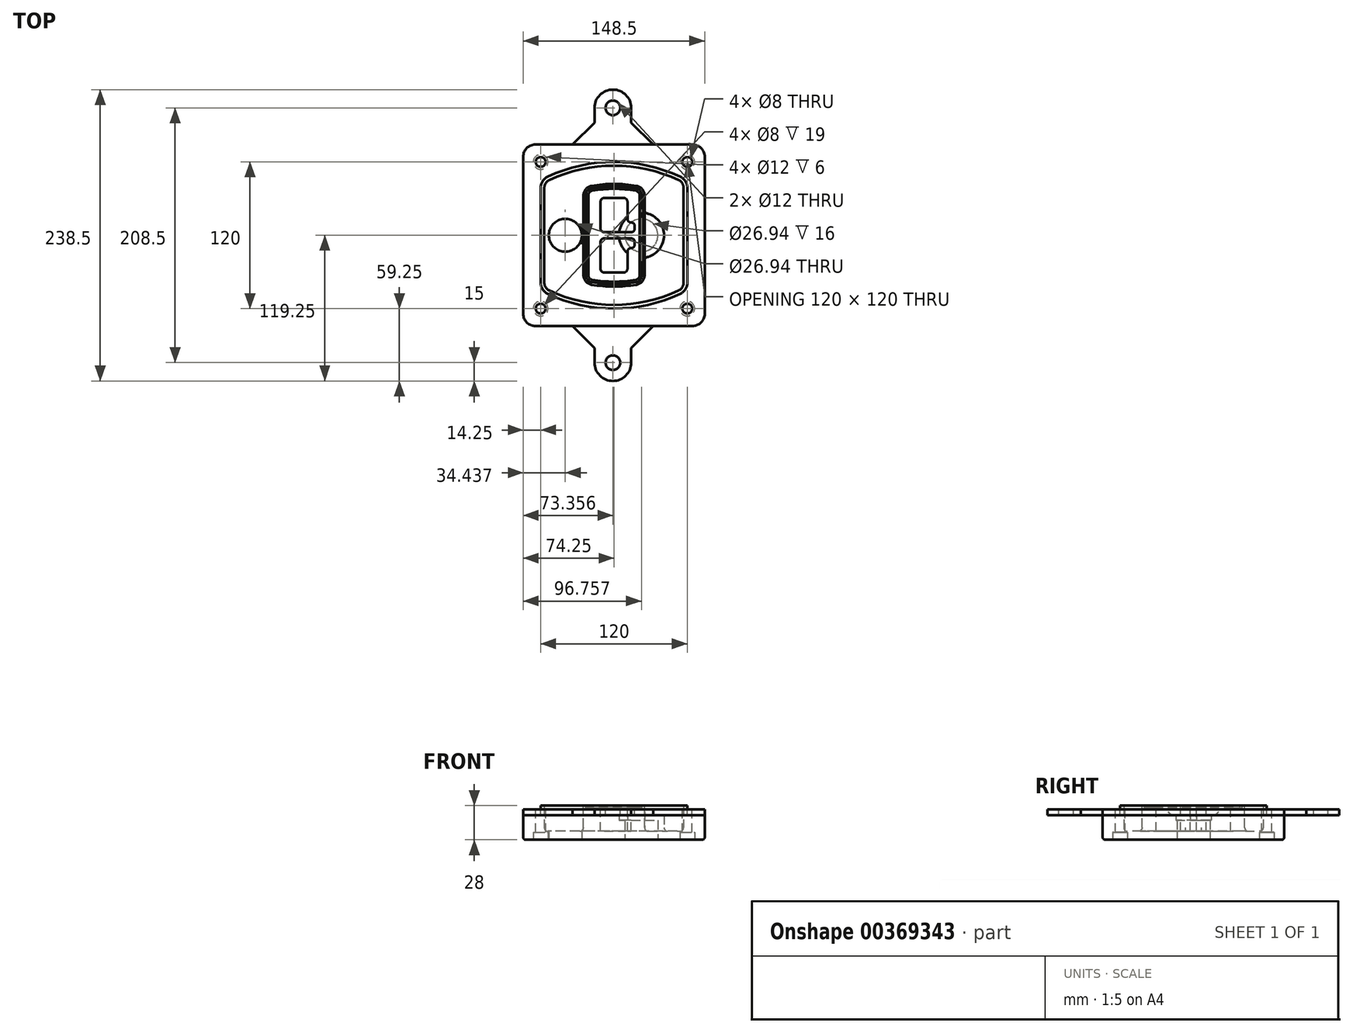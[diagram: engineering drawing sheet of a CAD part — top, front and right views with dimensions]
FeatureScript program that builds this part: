
annotation { "Feature Type Name" : "Feature", "Feature Type Description" : "" }
export const myFeature = defineFeature(function(context is Context, id is Id, definition is map)
    precondition{}
    {
        {
            var Q0;
            Q0=qCreatedBy(makeId("Top.planeOp"),FACE);
            var sketch = newSketch(context, id + "F0", { "sketchPlane" : qUnion([Q0])});
            skPoint(sketch, "E0.rect.middle", {"position": v(0, 0) * mm});
            skLineSegment(sketch, "E1.bottom", {"start": v(-64.25, -74.25) * mm, "end": v(64.25, -74.25) * mm});
            skLineSegment(sketch, "E1.top", {"start": v(-64.25, 74.25) * mm, "end": v(64.25, 74.25) * mm});
            skLineSegment(sketch, "E1.left", {"start": v(-74.25, -64.25) * mm, "end": v(-74.25, 64.25) * mm});
            skLineSegment(sketch, "E1.right", {"start": v(74.25, -64.25) * mm, "end": v(74.25, 64.25) * mm});
            skLineSegment(sketch, "E2", {"start": v(-74.25, 74.25) * mm, "end": v(74.25, -74.25) * mm, "construction": true});
            skLineSegment(sketch, "E3", {"start": v(74.25, 74.25) * mm, "end": v(-74.25, -74.25) * mm, "construction": true});
            skCircle(sketch, "E4", {"center": v(-60, 60) * mm, "radius": 4 * mm});
            skCircle(sketch, "E5", {"center": v(60, 60) * mm, "radius": 4 * mm});
            skCircle(sketch, "E6", {"center": v(60, -60) * mm, "radius": 4 * mm});
            skCircle(sketch, "E7", {"center": v(-60, -60) * mm, "radius": 4 * mm});
            skLineSegment(sketch, "E8", {"start": v(-60, 60) * mm, "end": v(60, 60) * mm, "construction": true});
            skLineSegment(sketch, "E9", {"start": v(60, 60) * mm, "end": v(60, -60) * mm, "construction": true});
            skLineSegment(sketch, "E10", {"start": v(60, -60) * mm, "end": v(-60, -60) * mm, "construction": true});
            skLineSegment(sketch, "E11", {"start": v(-60, -60) * mm, "end": v(-60, 60) * mm, "construction": true});
            skLineSegment(sketch, "E12", {"start": v(-60, 38.83) * mm, "end": v(-60, -38.83) * mm});
            skLineSegment(sketch, "E13", {"start": v(60, 38.83) * mm, "end": v(60, -38.83) * mm});
            skArc(sketch, "E14", {"start": v(54.26, 47.88) * mm, "mid": v(0, 60) * mm, "end": v(-54.26, 47.88) * mm});
            skArc(sketch, "E15", {"start": v(-54.26, -47.88) * mm, "mid": v(0, -60) * mm, "end": v(54.26, -47.88) * mm});
            skLineSegment(sketch, "E16", {"start": v(-60, 0) * mm, "end": v(60, 0) * mm, "construction": true});
            skPoint(sketch, "E17.visualSharp", {"position": v(-60, -45) * mm});
            skArc(sketch, "E17.filletArc", {"start": v(-60, -38.83) * mm, "mid": v(-58.44, -44.2) * mm, "end": v(-54.26, -47.88) * mm});
            skPoint(sketch, "E18.visualSharp", {"position": v(-60, 45) * mm});
            skArc(sketch, "E18.filletArc", {"start": v(-54.26, 47.88) * mm, "mid": v(-58.44, 44.2) * mm, "end": v(-60, 38.83) * mm});
            skPoint(sketch, "E19.visualSharp", {"position": v(60, 45) * mm});
            skArc(sketch, "E19.filletArc", {"start": v(60, 38.83) * mm, "mid": v(58.44, 44.2) * mm, "end": v(54.26, 47.88) * mm});
            skPoint(sketch, "E20.visualSharp", {"position": v(60, -45) * mm});
            skArc(sketch, "E20.filletArc", {"start": v(54.26, -47.88) * mm, "mid": v(58.44, -44.2) * mm, "end": v(60, -38.83) * mm});
            skPoint(sketch, "E21.visualSharp", {"position": v(-74.25, 74.25) * mm});
            skArc(sketch, "E21.filletArc", {"start": v(-64.25, 74.25) * mm, "mid": v(-71.32, 71.32) * mm, "end": v(-74.25, 64.25) * mm});
            skPoint(sketch, "E22.visualSharp", {"position": v(74.25, 74.25) * mm});
            skArc(sketch, "E22.filletArc", {"start": v(74.25, 64.25) * mm, "mid": v(71.32, 71.32) * mm, "end": v(64.25, 74.25) * mm});
            skPoint(sketch, "E23.visualSharp", {"position": v(74.25, -74.25) * mm});
            skArc(sketch, "E23.filletArc", {"start": v(64.25, -74.25) * mm, "mid": v(71.32, -71.32) * mm, "end": v(74.25, -64.25) * mm});
            skPoint(sketch, "E24.visualSharp", {"position": v(-74.25, -74.25) * mm});
            skArc(sketch, "E24.filletArc", {"start": v(-74.25, -64.25) * mm, "mid": v(-71.32, -71.32) * mm, "end": v(-64.25, -74.25) * mm});
            skArc(sketch, "E25.0", {"start": v(57, 38.83) * mm, "mid": v(55.9, 42.58) * mm, "end": v(52.98, 45.17) * mm});
            skLineSegment(sketch, "E25.1", {"start": v(57, 38.83) * mm, "end": v(57, -38.83) * mm});
            skArc(sketch, "E25.2", {"start": v(52.98, -45.17) * mm, "mid": v(55.9, -42.58) * mm, "end": v(57, -38.83) * mm});
            skArc(sketch, "E25.3", {"start": v(-52.98, -45.17) * mm, "mid": v(0, -57) * mm, "end": v(52.98, -45.17) * mm});
            skArc(sketch, "E25.4", {"start": v(-57, -38.83) * mm, "mid": v(-55.9, -42.58) * mm, "end": v(-52.98, -45.17) * mm});
            skArc(sketch, "E25.5", {"start": v(52.98, 45.17) * mm, "mid": v(0, 57) * mm, "end": v(-52.98, 45.17) * mm});
            skLineSegment(sketch, "E25.6", {"start": v(-57, 38.83) * mm, "end": v(-57, -38.83) * mm});
            skArc(sketch, "E25.7", {"start": v(-52.98, 45.17) * mm, "mid": v(-55.9, 42.58) * mm, "end": v(-57, 38.83) * mm});
            skArc(sketch, "E26.0", {"start": v(-55.96, 51.5) * mm, "mid": v(-61.82, 46.33) * mm, "end": v(-64, 38.83) * mm});
            skArc(sketch, "E26.1", {"start": v(55.96, 51.5) * mm, "mid": v(0, 64) * mm, "end": v(-55.96, 51.5) * mm});
            skArc(sketch, "E26.2", {"start": v(64, 38.83) * mm, "mid": v(61.82, 46.33) * mm, "end": v(55.96, 51.5) * mm});
            skLineSegment(sketch, "E26.3", {"start": v(64, 38.83) * mm, "end": v(64, -38.83) * mm});
            skArc(sketch, "E26.4", {"start": v(55.96, -51.5) * mm, "mid": v(61.82, -46.33) * mm, "end": v(64, -38.83) * mm});
            skLineSegment(sketch, "E26.5", {"start": v(-64, 38.83) * mm, "end": v(-64, -38.83) * mm});
            skArc(sketch, "E26.6", {"start": v(-55.96, -51.5) * mm, "mid": v(0, -64) * mm, "end": v(55.96, -51.5) * mm});
            skArc(sketch, "E26.7", {"start": v(-64, -38.83) * mm, "mid": v(-61.82, -46.33) * mm, "end": v(-55.96, -51.5) * mm});
            skSolve(sketch);
        }
        {
            var Q0;
            Q0=makeQuery(id+"F0.imprint","IMPRINT",FACE,{"disambiguationData":[TD([[makeQuery(id+"F0.imprint","IMPRINT",EDGE,{"derivedFrom":sQuery(id+"F0.wireOp",EDGE,"E1.bottom")}),1.0]])]});
            var Q1;
            Q1=makeQuery(id+"F0.imprint","IMPRINT",FACE,{"disambiguationData":[TD([[makeQuery(id+"F0.imprint","IMPRINT",EDGE,{"derivedFrom":sQuery(id+"F0.wireOp",EDGE,"E12")}),1.0]])]});
            var Q2;
            Q2=makeQuery(id+"F0.imprint","IMPRINT",FACE,{"disambiguationData":[TD([[makeQuery(id+"F0.imprint","IMPRINT",EDGE,{"derivedFrom":sQuery(id+"F0.wireOp",EDGE,"E25.0")}),1.0]])]});
            var Q3;
            Q3=makeQuery(id+"F0.imprint","IMPRINT",FACE,{"disambiguationData":[TD([[makeQuery(id+"F0.imprint","IMPRINT",EDGE,{"derivedFrom":sQuery(id+"F0.wireOp",EDGE,"E12")}),-1.0]])]});
            extrude(context, id + "F1", {"entities" : qUnion([Q0, Q1, Q2, Q3]), "oppositeDirection" : true, "depth" : 25 * mm});
        }
        {
            var Q0;
            Q0=makeQuery(id+"F0.imprint","IMPRINT",FACE,{"disambiguationData":[TD([[makeQuery(id+"F0.imprint","IMPRINT",EDGE,{"derivedFrom":sQuery(id+"F0.wireOp",EDGE,"E12")}),1.0]])]});
            extrude(context, id + "F2", {"entities" : qUnion([Q0]), "operationType" : NewBodyOperationType.ADD, "depth" : 3 * mm});
        }
        {
            var Q0;
            Q0=makeQuery(id+"F0.imprint","IMPRINT",FACE,{"disambiguationData":[TD([[makeQuery(id+"F0.imprint","IMPRINT",EDGE,{"derivedFrom":sQuery(id+"F0.wireOp",EDGE,"E25.0")}),1.0]])]});
            extrude(context, id + "F3", {"entities" : qUnion([Q0]), "operationType" : NewBodyOperationType.REMOVE, "oppositeDirection" : true, "depth" : 18 * mm});
        }
        {
            var Q0;
            Q0=makeQuery(id+"F2.opExtrude","CAP_FACE",FACE,{"disambiguationData":[OSD([sQuery(id+"F0.wireOp",EDGE,"E12"),sQuery(id+"F0.wireOp",EDGE,"E13"),sQuery(id+"F0.wireOp",EDGE,"E14"),sQuery(id+"F0.wireOp",EDGE,"E15"),sQuery(id+"F0.wireOp",EDGE,"E17.filletArc"),sQuery(id+"F0.wireOp",EDGE,"E18.filletArc"),sQuery(id+"F0.wireOp",EDGE,"E19.filletArc"),sQuery(id+"F0.wireOp",EDGE,"E20.filletArc"),sQuery(id+"F0.wireOp",EDGE,"E25.0"),sQuery(id+"F0.wireOp",EDGE,"E25.1"),sQuery(id+"F0.wireOp",EDGE,"E25.2"),sQuery(id+"F0.wireOp",EDGE,"E25.3"),sQuery(id+"F0.wireOp",EDGE,"E25.4"),sQuery(id+"F0.wireOp",EDGE,"E25.5"),sQuery(id+"F0.wireOp",EDGE,"E25.6"),sQuery(id+"F0.wireOp",EDGE,"E25.7")])],"isStart":false});
            var sketch = newSketch(context, id + "F4", { "sketchPlane" : qUnion([Q0])});
            skArc(sketch, "E27.0", {"start": v(-18.34, -40.45) * mm, "mid": v(0, -42) * mm, "end": v(18.34, -40.45) * mm});
            skArc(sketch, "E28.0", {"start": v(18.34, 40.45) * mm, "mid": v(0, 42) * mm, "end": v(-18.34, 40.45) * mm});
            skLineSegment(sketch, "E29", {"start": v(-25, 32.57) * mm, "end": v(-25, -32.57) * mm});
            skLineSegment(sketch, "E30", {"start": v(25, 32.57) * mm, "end": v(25, -32.57) * mm});
            skLineSegment(sketch, "E31", {"start": v(-25, 39.1) * mm, "end": v(25, 39.1) * mm, "construction": true});
            skLineSegment(sketch, "E32", {"start": v(-25, -39.1) * mm, "end": v(25, -39.1) * mm, "construction": true});
            skPoint(sketch, "E33.visualSharp", {"position": v(-25, 39.1) * mm});
            skArc(sketch, "E33.filletArc", {"start": v(-18.34, 40.45) * mm, "mid": v(-23.11, 37.73) * mm, "end": v(-25, 32.57) * mm});
            skPoint(sketch, "E34.visualSharp", {"position": v(25, 39.1) * mm});
            skArc(sketch, "E34.filletArc", {"start": v(25, 32.57) * mm, "mid": v(23.11, 37.73) * mm, "end": v(18.34, 40.45) * mm});
            skPoint(sketch, "E35.visualSharp", {"position": v(25, -39.1) * mm});
            skArc(sketch, "E35.filletArc", {"start": v(18.34, -40.45) * mm, "mid": v(23.11, -37.73) * mm, "end": v(25, -32.57) * mm});
            skPoint(sketch, "E36.visualSharp", {"position": v(-25, -39.1) * mm});
            skArc(sketch, "E36.filletArc", {"start": v(-25, -32.57) * mm, "mid": v(-23.11, -37.73) * mm, "end": v(-18.34, -40.45) * mm});
            skArc(sketch, "E37.0", {"start": v(52.98, 45.17) * mm, "mid": v(0, 57) * mm, "end": v(-52.98, 45.17) * mm});
            skArc(sketch, "E37.1", {"start": v(-52.98, 45.17) * mm, "mid": v(-55.9, 42.58) * mm, "end": v(-57, 38.83) * mm});
            skLineSegment(sketch, "E37.2", {"start": v(-57, 38.83) * mm, "end": v(-57, -38.83) * mm});
            skArc(sketch, "E37.3", {"start": v(-57, -38.83) * mm, "mid": v(-55.9, -42.58) * mm, "end": v(-52.98, -45.17) * mm});
            skArc(sketch, "E37.4", {"start": v(-52.98, -45.17) * mm, "mid": v(0, -57) * mm, "end": v(52.98, -45.17) * mm});
            skArc(sketch, "E37.5", {"start": v(52.98, -45.17) * mm, "mid": v(55.9, -42.58) * mm, "end": v(57, -38.83) * mm});
            skLineSegment(sketch, "E37.6", {"start": v(57, 38.83) * mm, "end": v(57, -38.83) * mm});
            skArc(sketch, "E37.7", {"start": v(57, 38.83) * mm, "mid": v(55.9, 42.58) * mm, "end": v(52.98, 45.17) * mm});
            skLineSegment(sketch, "E38.0", {"start": v(23, 32.57) * mm, "end": v(23, -32.57) * mm});
            skArc(sketch, "E38.1", {"start": v(18, -38.48) * mm, "mid": v(21.58, -36.44) * mm, "end": v(23, -32.57) * mm});
            skArc(sketch, "E38.2", {"start": v(-18, -38.48) * mm, "mid": v(0, -40) * mm, "end": v(18, -38.48) * mm});
            skArc(sketch, "E38.3", {"start": v(-23, -32.57) * mm, "mid": v(-21.58, -36.44) * mm, "end": v(-18, -38.48) * mm});
            skLineSegment(sketch, "E38.4", {"start": v(-23, 32.57) * mm, "end": v(-23, -32.57) * mm});
            skArc(sketch, "E38.5", {"start": v(23, 32.57) * mm, "mid": v(21.58, 36.44) * mm, "end": v(18, 38.48) * mm});
            skArc(sketch, "E38.6", {"start": v(-18, 38.48) * mm, "mid": v(-21.58, 36.44) * mm, "end": v(-23, 32.57) * mm});
            skArc(sketch, "E38.7", {"start": v(18, 38.48) * mm, "mid": v(0, 40) * mm, "end": v(-18, 38.48) * mm});
            skArc(sketch, "E39.0", {"start": v(21, 32.57) * mm, "mid": v(20.06, 35.15) * mm, "end": v(17.67, 36.5) * mm});
            skLineSegment(sketch, "E39.1", {"start": v(21, 32.57) * mm, "end": v(21, -32.57) * mm});
            skArc(sketch, "E39.2", {"start": v(17.67, -36.5) * mm, "mid": v(20.06, -35.15) * mm, "end": v(21, -32.57) * mm});
            skArc(sketch, "E39.3", {"start": v(-17.67, -36.5) * mm, "mid": v(0, -38) * mm, "end": v(17.67, -36.5) * mm});
            skArc(sketch, "E39.4", {"start": v(-21, -32.57) * mm, "mid": v(-20.06, -35.15) * mm, "end": v(-17.67, -36.5) * mm});
            skArc(sketch, "E39.5", {"start": v(17.67, 36.5) * mm, "mid": v(0, 38) * mm, "end": v(-17.67, 36.5) * mm});
            skLineSegment(sketch, "E39.6", {"start": v(-21, 32.57) * mm, "end": v(-21, -32.57) * mm});
            skArc(sketch, "E39.7", {"start": v(-17.67, 36.5) * mm, "mid": v(-20.06, 35.15) * mm, "end": v(-21, 32.57) * mm});
            skLineSegment(sketch, "E40", {"start": v(-25, 0) * mm, "end": v(25, 0) * mm, "construction": true});
            skLineSegment(sketch, "E41", {"start": v(-11, 5.5) * mm, "end": v(-11, 27.5) * mm});
            skLineSegment(sketch, "E42", {"start": v(-8, 30.5) * mm, "end": v(8, 30.5) * mm});
            skLineSegment(sketch, "E43", {"start": v(11, 27.5) * mm, "end": v(11, 13.5) * mm});
            skLineSegment(sketch, "E44", {"start": v(14, 10.5) * mm, "end": v(14, 10.5) * mm});
            skLineSegment(sketch, "E45", {"start": v(17, 7.5) * mm, "end": v(17, 5.5) * mm});
            skLineSegment(sketch, "E46", {"start": v(14, 2.5) * mm, "end": v(-8, 2.5) * mm});
            skPoint(sketch, "E47.visualSharp", {"position": v(-11, 30.5) * mm});
            skArc(sketch, "E47.filletArc", {"start": v(-8, 30.5) * mm, "mid": v(-10.12, 29.62) * mm, "end": v(-11, 27.5) * mm});
            skPoint(sketch, "E48.visualSharp", {"position": v(11, 30.5) * mm});
            skArc(sketch, "E48.filletArc", {"start": v(11, 27.5) * mm, "mid": v(10.12, 29.62) * mm, "end": v(8, 30.5) * mm});
            skPoint(sketch, "E49.visualSharp", {"position": v(11, 10.5) * mm});
            skArc(sketch, "E49.filletArc", {"start": v(11, 13.5) * mm, "mid": v(11.88, 11.38) * mm, "end": v(14, 10.5) * mm});
            skPoint(sketch, "E50.visualSharp", {"position": v(17, 10.5) * mm});
            skArc(sketch, "E50.filletArc", {"start": v(17, 7.5) * mm, "mid": v(16.12, 9.62) * mm, "end": v(14, 10.5) * mm});
            skPoint(sketch, "E51.visualSharp", {"position": v(17, 2.5) * mm});
            skArc(sketch, "E51.filletArc", {"start": v(14, 2.5) * mm, "mid": v(16.12, 3.38) * mm, "end": v(17, 5.5) * mm});
            skPoint(sketch, "E52.visualSharp", {"position": v(-11, 2.5) * mm});
            skArc(sketch, "E52.filletArc", {"start": v(-11, 5.5) * mm, "mid": v(-10.12, 3.38) * mm, "end": v(-8, 2.5) * mm});
            skLineSegment(sketch, "E53.0.MirrorCS", {"start": v(14, -2.5) * mm, "end": v(-8, -2.5) * mm});
            skArc(sketch, "E54.0.MirrorCS", {"start": v(-11, -5.5) * mm, "mid": v(-10.12, -3.38) * mm, "end": v(-8, -2.5) * mm});
            skLineSegment(sketch, "E55.0.MirrorCS", {"start": v(-11, -5.5) * mm, "end": v(-11, -27.5) * mm});
            skArc(sketch, "E56.0.MirrorCS", {"start": v(-8, -30.5) * mm, "mid": v(-10.12, -29.62) * mm, "end": v(-11, -27.5) * mm});
            skLineSegment(sketch, "E57.0.MirrorCS", {"start": v(-8, -30.5) * mm, "end": v(8, -30.5) * mm});
            skArc(sketch, "E58.0.MirrorCS", {"start": v(11, -27.5) * mm, "mid": v(10.12, -29.62) * mm, "end": v(8, -30.5) * mm});
            skLineSegment(sketch, "E59.0.MirrorCS", {"start": v(11, -27.5) * mm, "end": v(11, -13.5) * mm});
            skArc(sketch, "E60.0.MirrorCS", {"start": v(11, -13.5) * mm, "mid": v(11.88, -11.38) * mm, "end": v(14, -10.5) * mm});
            skArc(sketch, "E61.0.MirrorCS", {"start": v(17, -7.5) * mm, "mid": v(16.12, -9.62) * mm, "end": v(14, -10.5) * mm});
            skLineSegment(sketch, "E62.0.MirrorCS", {"start": v(17, -7.5) * mm, "end": v(17, -5.5) * mm});
            skArc(sketch, "E63.0.MirrorCS", {"start": v(14, -2.5) * mm, "mid": v(16.12, -3.38) * mm, "end": v(17, -5.5) * mm});
            skSolve(sketch);
        }
        {
            var Q0;
            Q0=makeQuery(id+"F4.imprint","IMPRINT",FACE,{"disambiguationData":[TD([[makeQuery(id+"F4.imprint","IMPRINT",EDGE,{"derivedFrom":sQuery(id+"F4.wireOp",EDGE,"E27.0")}),1.0]])]});
            var Q1;
            Q1=makeQuery(id+"F4.imprint","IMPRINT",FACE,{"disambiguationData":[TD([[makeQuery(id+"F4.imprint","IMPRINT",EDGE,{"derivedFrom":sQuery(id+"F4.wireOp",EDGE,"E38.0")}),-1.0]])]});
            var Q2;
            Q2=makeQuery(id+"F4.imprint","IMPRINT",FACE,{"disambiguationData":[TD([[makeQuery(id+"F4.imprint","IMPRINT",EDGE,{"derivedFrom":sQuery(id+"F4.wireOp",EDGE,"E39.0")}),1.0]])]});
            extrude(context, id + "F5", {"entities" : qUnion([Q0, Q1, Q2]), "operationType" : NewBodyOperationType.ADD, "endBound" : BoundingType.UP_TO_NEXT, "oppositeDirection" : true, "depth" : 25 * mm});
        }
        {
            var Q0;
            Q0=makeQuery(id+"F4.imprint","IMPRINT",FACE,{"disambiguationData":[TD([[makeQuery(id+"F4.imprint","IMPRINT",EDGE,{"derivedFrom":sQuery(id+"F4.wireOp",EDGE,"E38.0")}),-1.0]])]});
            extrude(context, id + "F6", {"entities" : qUnion([Q0]), "operationType" : NewBodyOperationType.REMOVE, "oppositeDirection" : true, "depth" : 2 * mm});
        }
        {
            var Q0;
            Q0=makeQuery(id+"F1.opExtrude","CAP_FACE",FACE,{"disambiguationData":[OSD([sQuery(id+"F0.wireOp",EDGE,"E1.bottom"),sQuery(id+"F0.wireOp",EDGE,"E1.top"),sQuery(id+"F0.wireOp",EDGE,"E1.left"),sQuery(id+"F0.wireOp",EDGE,"E1.right"),sQuery(id+"F0.wireOp",EDGE,"E4"),sQuery(id+"F0.wireOp",EDGE,"E5"),sQuery(id+"F0.wireOp",EDGE,"E6"),sQuery(id+"F0.wireOp",EDGE,"E7"),sQuery(id+"F0.wireOp",EDGE,"E21.filletArc"),sQuery(id+"F0.wireOp",EDGE,"E22.filletArc"),sQuery(id+"F0.wireOp",EDGE,"E23.filletArc"),sQuery(id+"F0.wireOp",EDGE,"E24.filletArc")])],"isStart":false});
            var sketch = newSketch(context, id + "F7", { "sketchPlane" : qUnion([Q0])});
            skCircle(sketch, "E64", {"center": v(22.5, 0) * mm, "radius": 13.47 * mm});
            skCircle(sketch, "E65", {"center": v(-39.81, 0) * mm, "radius": 13.47 * mm});
            skLineSegment(sketch, "E66", {"start": v(74.25, 0) * mm, "end": v(-74.25, 0) * mm});
            skCircle(sketch, "E67", {"center": v(22.5, 0) * mm, "radius": 18.47 * mm});
            skCircle(sketch, "E68", {"center": v(60, -60) * mm, "radius": 6 * mm});
            skCircle(sketch, "E69", {"center": v(-60, -60) * mm, "radius": 6 * mm});
            skCircle(sketch, "E70", {"center": v(-60, 60) * mm, "radius": 6 * mm});
            skCircle(sketch, "E71", {"center": v(60, 60) * mm, "radius": 6 * mm});
            skSolve(sketch);
        }
        {
            var Q0;
            {var subQ1=sQuery(id+"F7.wireOp",EDGE,"E66");var subQ4=sQuery(id+"F7.wireOp",EDGE,"E64");var subQ6=makeQuery(id+"F7.imprint","INTERSECT",VERTEX,{"disambiguationData":[OD(0.0)],"derivedFrom":[subQ4,subQ1]});Q0=makeQuery(id+"F7.imprint","IMPRINT",FACE,{"disambiguationData":[TD([[makeQuery(id+"F7.imprint","IMPRINT",EDGE,{"disambiguationData":[TD([[subQ6,-1.0]])],"derivedFrom":subQ4}),-1.0]])]});}
            var Q1;
            {var subQ0=sQuery(id+"F7.wireOp",EDGE,"E66");var subQ1=sQuery(id+"F7.wireOp",EDGE,"E64");var subQ3=makeQuery(id+"F7.imprint","INTERSECT",VERTEX,{"disambiguationData":[OD(0.0)],"derivedFrom":[subQ1,subQ0]});Q1=makeQuery(id+"F7.imprint","IMPRINT",FACE,{"disambiguationData":[TD([[makeQuery(id+"F7.imprint","IMPRINT",EDGE,{"disambiguationData":[TD([[subQ3,-1.0]])],"derivedFrom":subQ1}),1.0]])]});}
            var Q2;
            {var subQ0=sQuery(id+"F7.wireOp",EDGE,"E66");var subQ1=sQuery(id+"F7.wireOp",EDGE,"E64");var subQ3=makeQuery(id+"F7.imprint","INTERSECT",VERTEX,{"disambiguationData":[OD(0.0)],"derivedFrom":[subQ1,subQ0]});Q2=makeQuery(id+"F7.imprint","IMPRINT",FACE,{"disambiguationData":[TD([[makeQuery(id+"F7.imprint","IMPRINT",EDGE,{"disambiguationData":[TD([[subQ3,1.0]])],"derivedFrom":subQ1}),1.0]])]});}
            var Q3;
            {var subQ1=sQuery(id+"F7.wireOp",EDGE,"E66");var subQ4=sQuery(id+"F7.wireOp",EDGE,"E64");var subQ6=makeQuery(id+"F7.imprint","INTERSECT",VERTEX,{"disambiguationData":[OD(0.0)],"derivedFrom":[subQ4,subQ1]});Q3=makeQuery(id+"F7.imprint","IMPRINT",FACE,{"disambiguationData":[TD([[makeQuery(id+"F7.imprint","IMPRINT",EDGE,{"disambiguationData":[TD([[subQ6,1.0]])],"derivedFrom":subQ4}),-1.0]])]});}
            extrude(context, id + "F8", {"entities" : qUnion([Q0, Q1, Q2, Q3]), "operationType" : NewBodyOperationType.ADD, "oppositeDirection" : true, "depth" : 20 * mm});
        }
        {
            var Q0;
            {var subQ0=sQuery(id+"F7.wireOp",EDGE,"E66");var subQ1=sQuery(id+"F7.wireOp",EDGE,"E64");var subQ3=makeQuery(id+"F7.imprint","INTERSECT",VERTEX,{"disambiguationData":[OD(0.0)],"derivedFrom":[subQ1,subQ0]});Q0=makeQuery(id+"F7.imprint","IMPRINT",FACE,{"disambiguationData":[TD([[makeQuery(id+"F7.imprint","IMPRINT",EDGE,{"disambiguationData":[TD([[subQ3,-1.0]])],"derivedFrom":subQ1}),1.0]])]});}
            var Q1;
            {var subQ0=sQuery(id+"F7.wireOp",EDGE,"E66");var subQ1=sQuery(id+"F7.wireOp",EDGE,"E64");var subQ3=makeQuery(id+"F7.imprint","INTERSECT",VERTEX,{"disambiguationData":[OD(0.0)],"derivedFrom":[subQ1,subQ0]});Q1=makeQuery(id+"F7.imprint","IMPRINT",FACE,{"disambiguationData":[TD([[makeQuery(id+"F7.imprint","IMPRINT",EDGE,{"disambiguationData":[TD([[subQ3,1.0]])],"derivedFrom":subQ1}),1.0]])]});}
            extrude(context, id + "F9", {"entities" : qUnion([Q0, Q1]), "operationType" : NewBodyOperationType.REMOVE, "oppositeDirection" : true, "depth" : 16 * mm});
        }
        {
            var Q0;
            {var subQ0=sQuery(id+"F7.wireOp",EDGE,"E66");var subQ1=sQuery(id+"F7.wireOp",EDGE,"E65");var subQ3=makeQuery(id+"F7.imprint","INTERSECT",VERTEX,{"disambiguationData":[OD(0.0)],"derivedFrom":[subQ1,subQ0]});Q0=makeQuery(id+"F7.imprint","IMPRINT",FACE,{"disambiguationData":[TD([[makeQuery(id+"F7.imprint","IMPRINT",EDGE,{"disambiguationData":[TD([[subQ3,-1.0]])],"derivedFrom":subQ1}),1.0]])]});}
            var Q1;
            {var subQ0=sQuery(id+"F7.wireOp",EDGE,"E66");var subQ1=sQuery(id+"F7.wireOp",EDGE,"E65");var subQ3=makeQuery(id+"F7.imprint","INTERSECT",VERTEX,{"disambiguationData":[OD(0.0)],"derivedFrom":[subQ1,subQ0]});Q1=makeQuery(id+"F7.imprint","IMPRINT",FACE,{"disambiguationData":[TD([[makeQuery(id+"F7.imprint","IMPRINT",EDGE,{"disambiguationData":[TD([[subQ3,1.0]])],"derivedFrom":subQ1}),1.0]])]});}
            extrude(context, id + "F10", {"entities" : qUnion([Q0, Q1]), "operationType" : NewBodyOperationType.REMOVE, "oppositeDirection" : true, "depth" : 25 * mm});
        }
        {
            var Q0;
            Q0=makeQuery(id+"F7.imprint","IMPRINT",FACE,{"disambiguationData":[TD([[makeQuery(id+"F7.imprint","IMPRINT",EDGE,{"derivedFrom":sQuery(id+"F7.wireOp",EDGE,"E68")}),1.0]])]});
            var Q1;
            Q1=makeQuery(id+"F7.imprint","IMPRINT",FACE,{"disambiguationData":[TD([[makeQuery(id+"F7.imprint","IMPRINT",EDGE,{"derivedFrom":makeQuery(id+"F1.opExtrude","CAP_EDGE",EDGE,{"disambiguationData":[OSD([sQuery(id+"F0.wireOp",EDGE,"E5")])],"isStart":false})}),-1.0]])]});
            var Q2;
            Q2=makeQuery(id+"F7.imprint","IMPRINT",FACE,{"disambiguationData":[TD([[makeQuery(id+"F7.imprint","IMPRINT",EDGE,{"derivedFrom":sQuery(id+"F7.wireOp",EDGE,"E69")}),1.0]])]});
            var Q3;
            Q3=makeQuery(id+"F7.imprint","IMPRINT",FACE,{"disambiguationData":[TD([[makeQuery(id+"F7.imprint","IMPRINT",EDGE,{"derivedFrom":makeQuery(id+"F1.opExtrude","CAP_EDGE",EDGE,{"disambiguationData":[OSD([sQuery(id+"F0.wireOp",EDGE,"E4")])],"isStart":false})}),-1.0]])]});
            var Q4;
            Q4=makeQuery(id+"F7.imprint","IMPRINT",FACE,{"disambiguationData":[TD([[makeQuery(id+"F7.imprint","IMPRINT",EDGE,{"derivedFrom":sQuery(id+"F7.wireOp",EDGE,"E70")}),1.0]])]});
            var Q5;
            Q5=makeQuery(id+"F7.imprint","IMPRINT",FACE,{"disambiguationData":[TD([[makeQuery(id+"F7.imprint","IMPRINT",EDGE,{"derivedFrom":makeQuery(id+"F1.opExtrude","CAP_EDGE",EDGE,{"disambiguationData":[OSD([sQuery(id+"F0.wireOp",EDGE,"E7")])],"isStart":false})}),-1.0]])]});
            var Q6;
            Q6=makeQuery(id+"F7.imprint","IMPRINT",FACE,{"disambiguationData":[TD([[makeQuery(id+"F7.imprint","IMPRINT",EDGE,{"derivedFrom":sQuery(id+"F7.wireOp",EDGE,"E71")}),1.0]])]});
            var Q7;
            Q7=makeQuery(id+"F7.imprint","IMPRINT",FACE,{"disambiguationData":[TD([[makeQuery(id+"F7.imprint","IMPRINT",EDGE,{"derivedFrom":makeQuery(id+"F1.opExtrude","CAP_EDGE",EDGE,{"disambiguationData":[OSD([sQuery(id+"F0.wireOp",EDGE,"E6")])],"isStart":false})}),-1.0]])]});
            extrude(context, id + "F11", {"entities" : qUnion([Q0, Q1, Q2, Q3, Q4, Q5, Q6, Q7]), "operationType" : NewBodyOperationType.REMOVE, "oppositeDirection" : true, "depth" : 6 * mm});
        }
        {
            var Q0;
            Q0=makeQuery(id+"F9.boolean.opBoolean","COPY",FACE,{"derivedFrom":makeQuery(id+"F9.opExtrude","CAP_FACE",FACE,{"disambiguationData":[OSD([sQuery(id+"F7.wireOp",EDGE,"E64")])],"isStart":false})});
            var sketch = newSketch(context, id + "F12", { "sketchPlane" : qUnion([Q0])});
            skArc(sketch, "E72.0", {"start": v(11, 14.45) * mm, "mid": v(6.45, 9.13) * mm, "end": v(4.2, 2.5) * mm});
            skArc(sketch, "E72.1", {"start": v(4.2, -2.5) * mm, "mid": v(6.45, -9.13) * mm, "end": v(11, -14.45) * mm});
            skLineSegment(sketch, "E73", {"start": v(4.2, -2.5) * mm, "end": v(14, -2.5) * mm});
            skLineSegment(sketch, "E74.0", {"start": v(14, 2.5) * mm, "end": v(4.2, 2.5) * mm});
            skArc(sketch, "E74.1", {"start": v(14, 2.5) * mm, "mid": v(16.12, 3.38) * mm, "end": v(17, 5.5) * mm});
            skLineSegment(sketch, "E74.2", {"start": v(17, 7.5) * mm, "end": v(17, 5.5) * mm});
            skArc(sketch, "E74.3", {"start": v(17, 7.5) * mm, "mid": v(16.12, 9.62) * mm, "end": v(14, 10.5) * mm});
            skArc(sketch, "E74.4", {"start": v(11, 13.5) * mm, "mid": v(11.88, 11.38) * mm, "end": v(14, 10.5) * mm});
            skLineSegment(sketch, "E74.5", {"start": v(11, 14.45) * mm, "end": v(11, 13.5) * mm});
            skLineSegment(sketch, "E74.7", {"start": v(14, -2.5) * mm, "end": v(4.2, -2.5) * mm});
            skArc(sketch, "E74.8", {"start": v(14, -2.5) * mm, "mid": v(16.12, -3.38) * mm, "end": v(17, -5.5) * mm});
            skLineSegment(sketch, "E74.9", {"start": v(17, -7.5) * mm, "end": v(17, -5.5) * mm});
            skArc(sketch, "E74.10", {"start": v(17, -7.5) * mm, "mid": v(16.12, -9.62) * mm, "end": v(14, -10.5) * mm});
            skArc(sketch, "E74.11", {"start": v(11, -13.5) * mm, "mid": v(11.88, -11.38) * mm, "end": v(14, -10.5) * mm});
            skLineSegment(sketch, "E74.12", {"start": v(11, -14.45) * mm, "end": v(11, -13.5) * mm});
            skPoint(sketch, "E75.orphan", {"position": v(11, -27.5) * mm});
            skPoint(sketch, "E76.orphan", {"position": v(-8, -2.5) * mm});
            skPoint(sketch, "E77.orphan", {"position": v(-8, 2.5) * mm});
            skPoint(sketch, "E78.orphan", {"position": v(11, 27.5) * mm});
            skSolve(sketch);
        }
        {
            var Q0;
            {var subQ7=sQuery(id+"F12.wireOp",EDGE,"E72.0");var subQ14=sQuery(id+"F12.wireOp",EDGE,"E72.1");var subQ16=sQuery(id+"F12.wireOp",EDGE,"E74.1");var subQ18=sQuery(id+"F12.wireOp",EDGE,"E74.8");Q0=qUnion([makeQuery(id+"F12.imprint","IMPRINT",FACE,{"disambiguationData":[TD([[makeQuery(id+"F12.imprint","IMPRINT",EDGE,{"derivedFrom":subQ7}),1.0]])]}),makeQuery(id+"F12.imprint","IMPRINT",FACE,{"disambiguationData":[TD([[makeQuery(id+"F12.imprint","IMPRINT",EDGE,{"derivedFrom":subQ14}),1.0]])]}),makeQuery(id+"F12.imprint","IMPRINT",FACE,{"disambiguationData":[TD([[makeQuery(id+"F12.imprint","IMPRINT",EDGE,{"derivedFrom":subQ16}),1.0]])]}),makeQuery(id+"F12.imprint","IMPRINT",FACE,{"disambiguationData":[TD([[makeQuery(id+"F12.imprint","IMPRINT",EDGE,{"derivedFrom":subQ18}),-1.0]])]})]);}
            var Q1;
            Q1=makeQuery(id+"F5.boolean.opBoolean","SPLIT",FACE,{"disambiguationData":[TD([makeQuery(id+"F5.opExtrude","SWEPT_FACE",FACE,{"disambiguationData":[OSD([sQuery(id+"F4.wireOp",EDGE,"E41")])]})])],"derivedFrom":makeQuery(id+"F3.boolean.opBoolean","COPY",FACE,{"derivedFrom":makeQuery(id+"F3.opExtrude","CAP_FACE",FACE,{"disambiguationData":[OSD([sQuery(id+"F0.wireOp",EDGE,"E25.0"),sQuery(id+"F0.wireOp",EDGE,"E25.1"),sQuery(id+"F0.wireOp",EDGE,"E25.2"),sQuery(id+"F0.wireOp",EDGE,"E25.3"),sQuery(id+"F0.wireOp",EDGE,"E25.4"),sQuery(id+"F0.wireOp",EDGE,"E25.5"),sQuery(id+"F0.wireOp",EDGE,"E25.6"),sQuery(id+"F0.wireOp",EDGE,"E25.7")])],"isStart":false})})});
            extrude(context, id + "F13", {"entities" : qUnion([Q0]), "operationType" : NewBodyOperationType.REMOVE, "endBound" : BoundingType.UP_TO_SURFACE, "endBoundEntityFace" : qUnion([Q1]), "depth" : 25 * mm});
        }
        {
            var Q0;
            Q0=makeQuery(id+"F3.boolean.opBoolean","COPY",EDGE,{"derivedFrom":makeQuery(id+"F3.opExtrude","CAP_EDGE",EDGE,{"disambiguationData":[OSD([sQuery(id+"F0.wireOp",EDGE,"E25.6")])],"isStart":false})});
            var Q1;
            Q1=makeQuery(id+"F8.boolean.opBoolean","INTERSECT",EDGE,{"derivedFrom":[makeQuery(id+"F5.opExtrude","SWEPT_FACE",FACE,{"disambiguationData":[OSD([sQuery(id+"F4.wireOp",EDGE,"E30")])]}),makeQuery(id+"F8.opExtrude","CAP_FACE",FACE,{"disambiguationData":[OSD([sQuery(id+"F7.wireOp",EDGE,"E67")])],"isStart":false})]});
            var Q2;
            Q2=makeQuery(id+"F8.boolean.opBoolean","INTERSECT",EDGE,{"disambiguationData":[OD(1.0)],"derivedFrom":[makeQuery(id+"F5.opExtrude","SWEPT_FACE",FACE,{"disambiguationData":[OSD([sQuery(id+"F4.wireOp",EDGE,"E30")])]}),makeQuery(id+"F8.opExtrude","SWEPT_FACE",FACE,{"disambiguationData":[OSD([sQuery(id+"F7.wireOp",EDGE,"E67")])]})]});
            var Q3;
            {var subQ0=sQuery(id+"F4.wireOp",EDGE,"E30");Q3=makeQuery(id+"F8.boolean.opBoolean","SPLIT",EDGE,{"disambiguationData":[TD([makeQuery(id+"F5.opExtrude","SWEPT_FACE",FACE,{"disambiguationData":[OSD([sQuery(id+"F4.wireOp",EDGE,"E35.filletArc")])]})])],"derivedFrom":makeQuery(id+"F5.opExtrude","CAP_EDGE",EDGE,{"disambiguationData":[OSD([subQ0])],"isStart":false})});}
            var Q4;
            {var subQ0=sQuery(id+"F0.wireOp",EDGE,"E25.7");var subQ1=sQuery(id+"F0.wireOp",EDGE,"E25.1");var subQ2=sQuery(id+"F0.wireOp",EDGE,"E25.6");var subQ3=sQuery(id+"F0.wireOp",EDGE,"E25.5");var subQ4=sQuery(id+"F0.wireOp",EDGE,"E25.4");var subQ5=sQuery(id+"F0.wireOp",EDGE,"E25.0");var subQ6=sQuery(id+"F0.wireOp",EDGE,"E25.2");var subQ7=sQuery(id+"F0.wireOp",EDGE,"E25.3");Q4=makeQuery(id+"F8.boolean.opBoolean","INTERSECT",EDGE,{"derivedFrom":[makeQuery(id+"F5.boolean.opBoolean","SPLIT",FACE,{"disambiguationData":[TD([makeQuery(id+"F2.opExtrude","SWEPT_FACE",FACE,{"disambiguationData":[OSD([subQ5])]})])],"derivedFrom":makeQuery(id+"F3.boolean.opBoolean","COPY",FACE,{"derivedFrom":makeQuery(id+"F3.opExtrude","CAP_FACE",FACE,{"disambiguationData":[OSD([subQ5,subQ1,subQ6,subQ7,subQ4,subQ3,subQ2,subQ0])],"isStart":false})})}),makeQuery(id+"F8.opExtrude","SWEPT_FACE",FACE,{"disambiguationData":[OSD([sQuery(id+"F7.wireOp",EDGE,"E67")])]})]});}
            var Q5;
            Q5=makeQuery(id+"F8.boolean.opBoolean","INTERSECT",EDGE,{"disambiguationData":[OD(0.0)],"derivedFrom":[makeQuery(id+"F5.opExtrude","SWEPT_FACE",FACE,{"disambiguationData":[OSD([sQuery(id+"F4.wireOp",EDGE,"E30")])]}),makeQuery(id+"F8.opExtrude","SWEPT_FACE",FACE,{"disambiguationData":[OSD([sQuery(id+"F7.wireOp",EDGE,"E67")])]})]});
            fillet(context, id + "F14", {"entities" : qUnion([Q0, Q1, Q2, Q3, Q4, Q5]), "radius" : 3 * mm, "tangentPropagation" : true, "allowEdgeOverflow" : false});
        }
        {
            var Q0;
            Q0=makeQuery(id+"F1.opExtrude","CAP_EDGE",EDGE,{"disambiguationData":[OSD([sQuery(id+"F0.wireOp",EDGE,"E1.bottom")])],"isStart":false});
            fillet(context, id + "F15", {"entities" : qUnion([Q0]), "radius" : 2 * mm, "tangentPropagation" : true, "allowEdgeOverflow" : false});
        }
        {
            var Q0;
            {var subQ0=sQuery(id+"F0.wireOp",EDGE,"E21.filletArc");var subQ1=sQuery(id+"F0.wireOp",EDGE,"E7");var subQ2=sQuery(id+"F0.wireOp",EDGE,"E6");var subQ3=sQuery(id+"F0.wireOp",EDGE,"E5");var subQ4=sQuery(id+"F0.wireOp",EDGE,"E4");var subQ5=sQuery(id+"F0.wireOp",EDGE,"E22.filletArc");var subQ6=sQuery(id+"F0.wireOp",EDGE,"E1.bottom");var subQ7=sQuery(id+"F0.wireOp",EDGE,"E1.right");var subQ8=sQuery(id+"F0.wireOp",EDGE,"E1.top");var subQ9=sQuery(id+"F0.wireOp",EDGE,"E1.left");var subQ10=sQuery(id+"F0.wireOp",EDGE,"E23.filletArc");var subQ11=sQuery(id+"F0.wireOp",EDGE,"E24.filletArc");Q0=makeQuery(id+"F2.boolean.opBoolean","SPLIT",FACE,{"disambiguationData":[TD([makeQuery(id+"F1.opExtrude","SWEPT_FACE",FACE,{"disambiguationData":[OSD([subQ6])]})])],"derivedFrom":makeQuery(id+"F1.opExtrude","CAP_FACE",FACE,{"disambiguationData":[OSD([subQ6,subQ8,subQ9,subQ7,subQ4,subQ3,subQ2,subQ1,subQ0,subQ5,subQ10,subQ11])],"isStart":true})});}
            var sketch = newSketch(context, id + "F16", { "sketchPlane" : qUnion([Q0])});
            skLineSegment(sketch, "E79", {"start": v(14.1, 92.25) * mm, "end": v(14.1, 104.25) * mm});
            skLineSegment(sketch, "E80", {"start": v(-15.9, 92.25) * mm, "end": v(-15.9, 104.25) * mm});
            skArc(sketch, "E81", {"start": v(14.1, 104.25) * mm, "mid": v(-0.9, 119.25) * mm, "end": v(-15.9, 104.25) * mm});
            skCircle(sketch, "E82", {"center": v(-0.9, 104.25) * mm, "radius": 6 * mm});
            skLineSegment(sketch, "E83", {"start": v(-0.9, 104.25) * mm, "end": v(0, 74.25) * mm, "construction": true});
            skLineSegment(sketch, "E84", {"start": v(-15.9, 92.25) * mm, "end": v(-33.9, 74.25) * mm});
            skLineSegment(sketch, "E85", {"start": v(14.1, 92.25) * mm, "end": v(32.1, 74.25) * mm});
            skLineSegment(sketch, "E86", {"start": v(-15.9, -92.25) * mm, "end": v(-15.9, -104.25) * mm});
            skLineSegment(sketch, "E87", {"start": v(14.1, -92.25) * mm, "end": v(14.1, -104.25) * mm});
            skArc(sketch, "E88", {"start": v(-15.9, -104.25) * mm, "mid": v(-0.9, -119.25) * mm, "end": v(14.1, -104.25) * mm});
            skCircle(sketch, "E89", {"center": v(-0.9, -104.25) * mm, "radius": 6 * mm});
            skLineSegment(sketch, "E90", {"start": v(-0.9, -104.25) * mm, "end": v(-1.79, -74.25) * mm, "construction": true});
            skLineSegment(sketch, "E91", {"start": v(14.1, -92.25) * mm, "end": v(32.1, -74.25) * mm});
            skLineSegment(sketch, "E92", {"start": v(-15.9, -92.25) * mm, "end": v(-33.9, -74.25) * mm});
            skSolve(sketch);
        }
        {
            var Q0;
            Q0=makeQuery(id+"F16.imprint","IMPRINT",FACE,{"disambiguationData":[TD([[makeQuery(id+"F16.imprint","IMPRINT",EDGE,{"derivedFrom":sQuery(id+"F16.wireOp",EDGE,"E79")}),1.0]])]});
            var Q1;
            Q1=makeQuery(id+"F16.imprint","IMPRINT",FACE,{"disambiguationData":[TD([[makeQuery(id+"F16.imprint","IMPRINT",EDGE,{"derivedFrom":sQuery(id+"F16.wireOp",EDGE,"E86")}),1.0]])]});
            var Q2;
            Q2=makeQuery(id+"F16.imprint","IMPRINT",FACE,{"disambiguationData":[TD([[makeQuery(id+"F16.imprint","IMPRINT",EDGE,{"derivedFrom":makeQuery(id+"F1.opExtrude","CAP_EDGE",EDGE,{"disambiguationData":[OSD([sQuery(id+"F0.wireOp",EDGE,"E1.left")])],"isStart":true})}),-1.0]])]});
            extrude(context, id + "F17", {"entities" : qUnion([Q0, Q1, Q2]), "oppositeDirection" : true, "depth" : 5 * mm});
        }
    });
